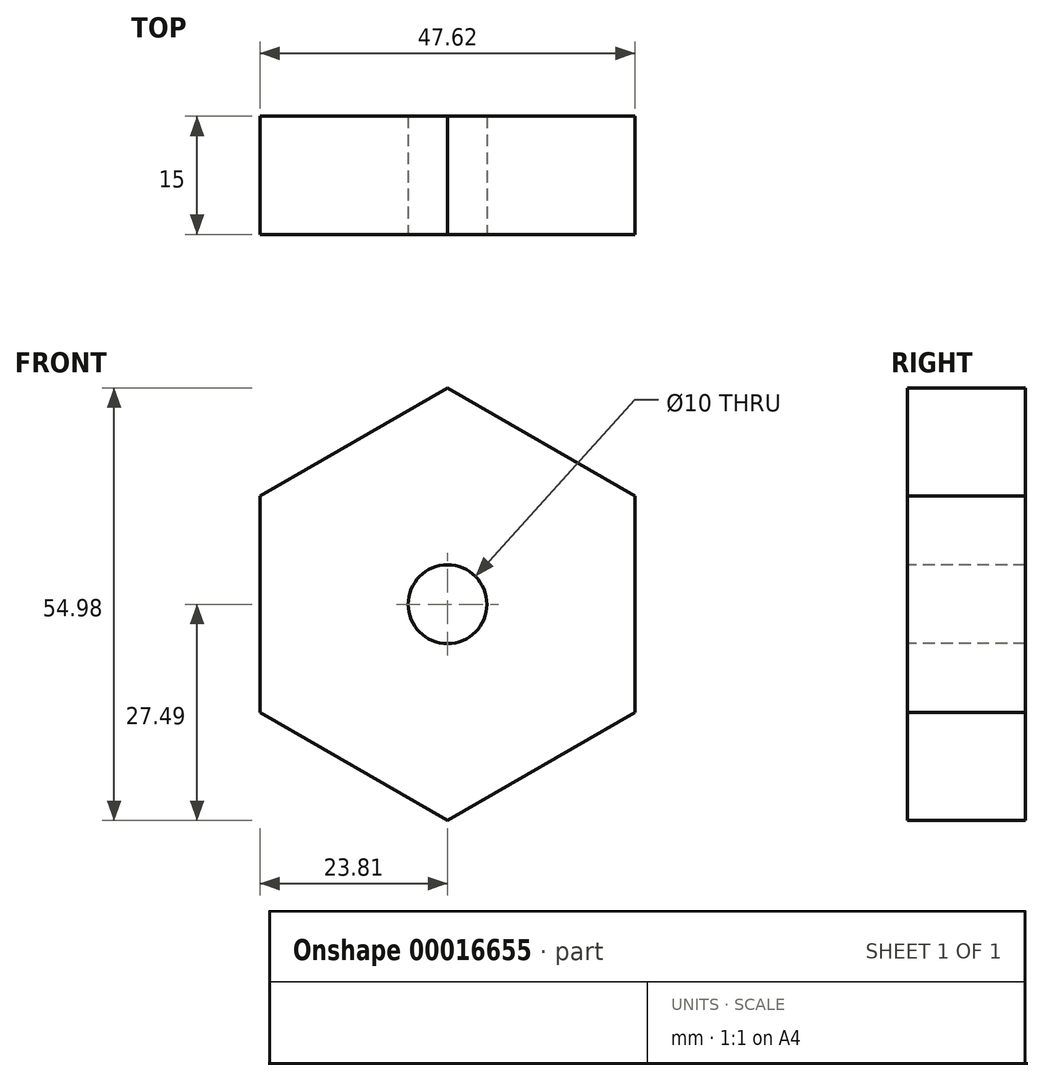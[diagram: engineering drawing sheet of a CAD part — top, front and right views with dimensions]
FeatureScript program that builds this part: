
annotation { "Feature Type Name" : "Feature", "Feature Type Description" : "" }
export const myFeature = defineFeature(function(context is Context, id is Id, definition is map)
    precondition{}
    {
        {
            var Q0;
            Q0=qCreatedBy(makeId("Front.planeOp"),FACE);
            var sketch = newSketch(context, id + "F0", { "sketchPlane" : qUnion([Q0])});
            skCircle(sketch, "E0.cCircle", {"center": v(0, 0) * mm, "radius": 27.5 * mm, "construction": true});
            skLineSegment(sketch, "E0.0", {"start": v(-23.8, -13.75) * mm, "end": v(-23.8, 13.75) * mm});
            skLineSegment(sketch, "E0.1", {"start": v(-23.8, 13.75) * mm, "end": v(0, 27.5) * mm});
            skLineSegment(sketch, "E0.2", {"start": v(0, 27.5) * mm, "end": v(23.8, 13.75) * mm});
            skLineSegment(sketch, "E0.3", {"start": v(23.8, 13.75) * mm, "end": v(23.8, -13.75) * mm});
            skLineSegment(sketch, "E0.4", {"start": v(23.8, -13.75) * mm, "end": v(0, -27.5) * mm});
            skLineSegment(sketch, "E0.5", {"start": v(0, -27.5) * mm, "end": v(-23.8, -13.75) * mm});
            skSolve(sketch);
        }
        {
            var Q0;
            Q0 = qSketchRegion(id + "F0", true);
            extrude(context, id + "F1", {"entities" : qUnion([Q0]), "depth" : 15 * mm});
        }
        {
            var Q0;
            Q0=makeQuery(id+"F1.opExtrude","CAP_FACE",FACE,{"disambiguationData":[OSD([sQuery(id+"F0.wireOp",EDGE,"E0.0"),sQuery(id+"F0.wireOp",EDGE,"E0.1"),sQuery(id+"F0.wireOp",EDGE,"E0.2"),sQuery(id+"F0.wireOp",EDGE,"E0.3"),sQuery(id+"F0.wireOp",EDGE,"E0.4"),sQuery(id+"F0.wireOp",EDGE,"E0.5")])],"isStart":false});
            var sketch = newSketch(context, id + "F2", { "sketchPlane" : qUnion([Q0])});
            skCircle(sketch, "E1", {"center": v(0, 0) * mm, "radius": 5 * mm});
            skSolve(sketch);
        }
        {
            var Q0;
            Q0 = qSketchRegion(id + "F2", true);
            extrude(context, id + "F3", {"entities" : qUnion([Q0]), "operationType" : NewBodyOperationType.REMOVE, "endBound" : BoundingType.THROUGH_ALL, "oppositeDirection" : true, "depth" : 25 * mm});
        }
    });
